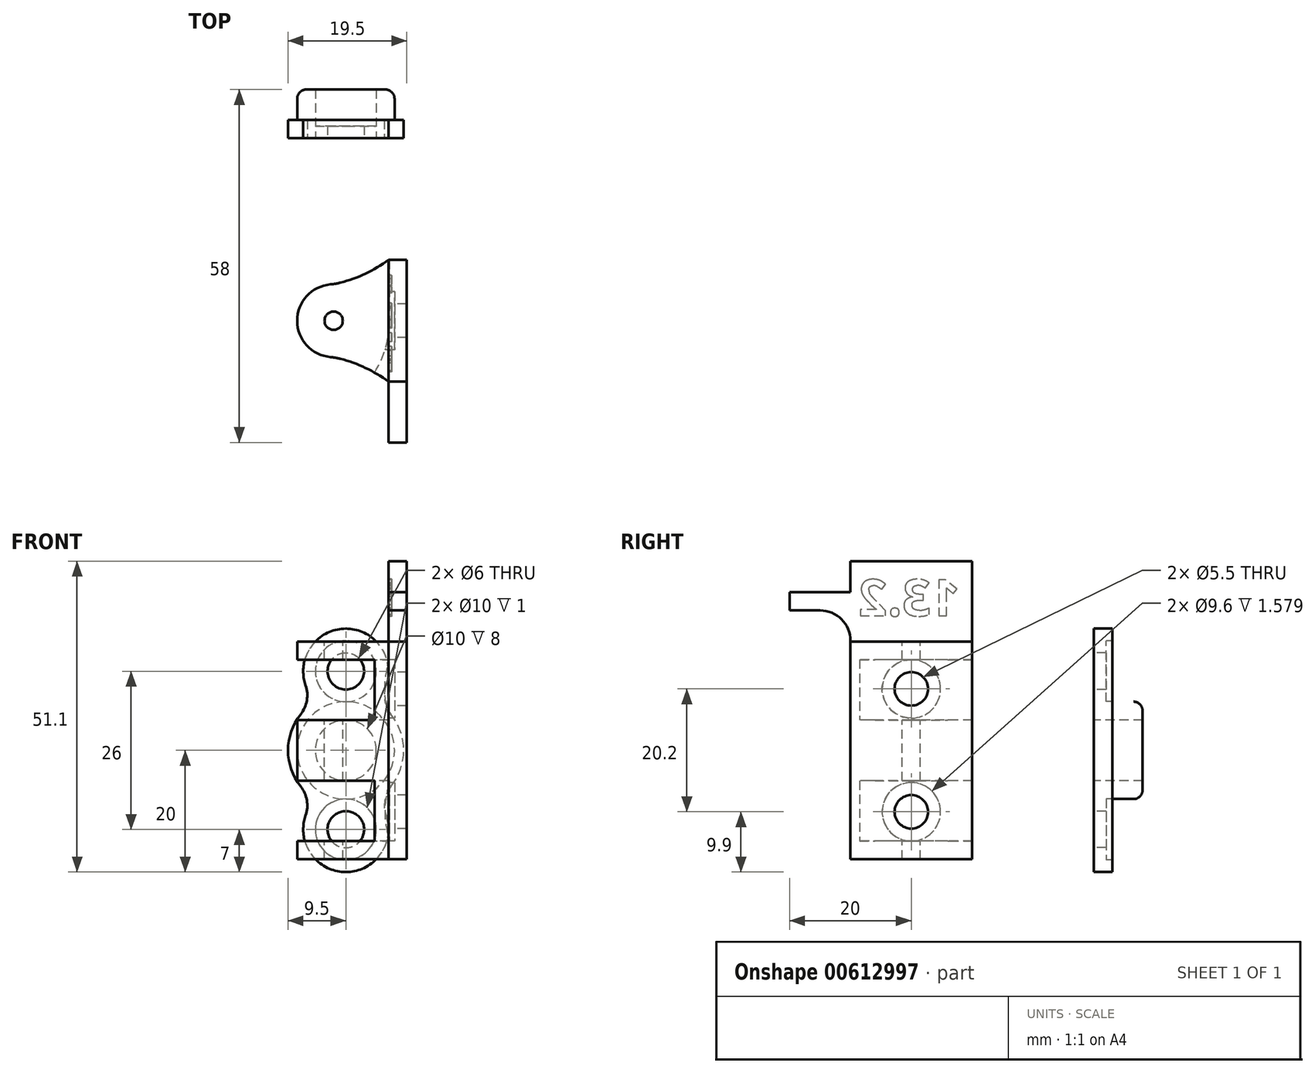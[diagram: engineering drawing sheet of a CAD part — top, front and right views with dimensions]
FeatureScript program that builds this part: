
annotation { "Feature Type Name" : "Feature", "Feature Type Description" : "" }
export const myFeature = defineFeature(function(context is Context, id is Id, definition is map)
    precondition{}
    {
        {
            var Q0;
            Q0=qCreatedBy(makeId("Top.planeOp"),FACE);
            var sketch = newSketch(context, id + "F0", { "sketchPlane" : qUnion([Q0])});
            skLineSegment(sketch, "E0", {"start": v(0, 0) * mm, "end": v(0, 17) * mm});
            skLineSegment(sketch, "E1", {"start": v(0, 17) * mm, "end": v(-3, 17) * mm});
            skLineSegment(sketch, "E2", {"start": v(-3, 17) * mm, "end": v(-3, -3) * mm});
            skLineSegment(sketch, "E3", {"start": v(-3, -3) * mm, "end": v(17, -3) * mm});
            skLineSegment(sketch, "E4", {"start": v(17, -3) * mm, "end": v(17, 0) * mm});
            skLineSegment(sketch, "E5", {"start": v(17, 0) * mm, "end": v(0, 0) * mm});
            skLineSegment(sketch, "E6", {"start": v(0, 0) * mm, "end": v(0, -3) * mm});
            skPoint(sketch, "E6.endSnap0", {"position": v(7, -3) * mm});
            skSolve(sketch);
        }
        {
            var Q0;
            Q0=makeQuery(id+"F0.imprint","IMPRINT",FACE,{"disambiguationData":[TD([[makeQuery(id+"F0.imprint","IMPRINT",EDGE,{"derivedFrom":sQuery(id+"F0.wireOp",EDGE,"E0")}),1.0]])]});
            extrude(context, id + "F1", {"entities" : qUnion([Q0]), "endBound" : BoundingType.SYMMETRIC, "depth" : 35.8 * mm, "offsetDistance" : 25 * mm});
        }
        {
            var Q0;
            Q0=makeQuery(id+"F1.opExtrude","CAP_FACE",FACE,{"disambiguationData":[OSD([sQuery(id+"F0.wireOp",EDGE,"E0"),sQuery(id+"F0.wireOp",EDGE,"E1"),sQuery(id+"F0.wireOp",EDGE,"E2"),sQuery(id+"F0.wireOp",EDGE,"E3"),sQuery(id+"F0.wireOp",EDGE,"E4"),sQuery(id+"F0.wireOp",EDGE,"E5")])],"isStart":false});
            var sketch = newSketch(context, id + "F2", { "sketchPlane" : qUnion([Q0])});
            skCircle(sketch, "E7", {"center": v(-12, 7) * mm, "radius": 6 * mm});
            skLineSegment(sketch, "E8", {"start": v(-3, 7) * mm, "end": v(-45.71, 7) * mm, "construction": true});
            skArc(sketch, "E9", {"start": v(-3, -3) * mm, "mid": v(-7.28, -0.51) * mm, "end": v(-12, 1) * mm});
            skArc(sketch, "E10.MirrorCS", {"start": v(-3, 17) * mm, "mid": v(-7.28, 14.51) * mm, "end": v(-12, 13) * mm});
            skCircle(sketch, "E11", {"center": v(-12, 7) * mm, "radius": 5 * mm, "construction": true});
            skSolve(sketch);
        }
        {
            var Q0;
            Q0 = qSketchRegion(id + "F2", true);
            var Q1;
            {var subQ5=makeQuery(id+"F1.opExtrude","CAP_EDGE",EDGE,{"disambiguationData":[OSD([sQuery(id+"F0.wireOp",EDGE,"E2")])],"isStart":false});Q1=makeQuery(id+"F2.imprint","IMPRINT",FACE,{"disambiguationData":[TD([[makeQuery(id+"F2.imprint","IMPRINT",EDGE,{"derivedFrom":subQ5}),-1.0]])]});}
            var Q2;
            Q2=makeQuery(id+"F1.opExtrude","CAP_FACE",FACE,{"disambiguationData":[OSD([sQuery(id+"F0.wireOp",EDGE,"E0"),sQuery(id+"F0.wireOp",EDGE,"E1"),sQuery(id+"F0.wireOp",EDGE,"E2"),sQuery(id+"F0.wireOp",EDGE,"E3"),sQuery(id+"F0.wireOp",EDGE,"E4"),sQuery(id+"F0.wireOp",EDGE,"E5")])],"isStart":true});
            extrude(context, id + "F3", {"entities" : qUnion([Q0, Q1]), "operationType" : NewBodyOperationType.ADD, "endBound" : BoundingType.UP_TO_SURFACE, "oppositeDirection" : true, "depth" : 25 * mm, "endBoundEntityFace" : qUnion([Q2]), "offsetDistance" : 25 * mm});
        }
        {
            var Q0;
            Q0=sQuery(id+"F2.wireOp",VERTEX,"E7.center");
            var Q1;
            Q1=qCreatedBy(makeId("Front.planeOp"),FACE);
            cPlane(context, id + "F4", {"entities" : qUnion([Q0, Q1]), "cplaneType" : CPlaneType.PLANE_POINT, "offset" : 25 * mm, "width" : 150 * mm, "height" : 150 * mm});
        }
        {
            var Q0;
            Q0=qCreatedBy(id+"F4.planeOp",FACE);
            var sketch = newSketch(context, id + "F5", { "sketchPlane" : qUnion([Q0])});
            skLineSegment(sketch, "E12", {"start": v(-27.2, 0) * mm, "end": v(27.2, 0) * mm, "construction": true});
            skLineSegment(sketch, "E13", {"start": v(-12, 17.9) * mm, "end": v(-12, -24.98) * mm, "construction": true});
            skLineSegment(sketch, "E14", {"start": v(0, 17.9) * mm, "end": v(0, -24.98) * mm, "construction": true});
            skLineSegment(sketch, "E15", {"start": v(-2.85, 17.9) * mm, "end": v(-2.85, -24.98) * mm, "construction": true});
            skLineSegment(sketch, "E16", {"start": v(-2.85, 14.9) * mm, "end": v(-19.05, 14.9) * mm});
            skLineSegment(sketch, "E17", {"start": v(-19.05, 14.9) * mm, "end": v(-19.05, 5) * mm});
            skLineSegment(sketch, "E18", {"start": v(-19.05, 5) * mm, "end": v(-2.85, 5) * mm});
            skLineSegment(sketch, "E19", {"start": v(-2.85, 5) * mm, "end": v(-2.85, 14.9) * mm});
            skLineSegment(sketch, "E20.MirrorCS", {"start": v(-19.05, -5) * mm, "end": v(-2.85, -5) * mm});
            skLineSegment(sketch, "E21.MirrorCS", {"start": v(-19.05, -14.9) * mm, "end": v(-19.05, -5) * mm});
            skLineSegment(sketch, "E22.MirrorCS", {"start": v(-2.85, -14.9) * mm, "end": v(-19.05, -14.9) * mm});
            skLineSegment(sketch, "E23.MirrorCS", {"start": v(-2.85, -17.9) * mm, "end": v(-2.85, 24.98) * mm, "construction": true});
            skLineSegment(sketch, "E24", {"start": v(0, -17.9) * mm, "end": v(-25.22, -17.9) * mm, "construction": true});
            skLineSegment(sketch, "E25", {"start": v(-2.85, -5) * mm, "end": v(-2.85, -14.9) * mm});
            skSolve(sketch);
        }
        {
            var Q0;
            Q0=makeQuery(id+"F5.imprint","IMPRINT",FACE,{"disambiguationData":[TD([[makeQuery(id+"F5.imprint","IMPRINT",EDGE,{"derivedFrom":sQuery(id+"F5.wireOp",EDGE,"E16")}),1.0]])]});
            var Q1;
            Q1=makeQuery(id+"F5.imprint","IMPRINT",FACE,{"disambiguationData":[TD([[makeQuery(id+"F5.imprint","IMPRINT",EDGE,{"derivedFrom":sQuery(id+"F5.wireOp",EDGE,"E20.MirrorCS")}),-1.0]])]});
            var Q2;
            Q2=sQuery(id+"F5.wireOp",EDGE,"E17");
            revolve(context, id + "F6", {"operationType" : NewBodyOperationType.REMOVE, "surfaceOperationType" : NewSurfaceOperationType.NEW, "entities" : qUnion([Q0, Q1]), "axis" : qUnion([Q2]), "revolveType" : RevolveType.FULL, "oppositeDirection" : true});
        }
        {
            var Q0;
            Q0=makeQuery(id+"F5.imprint","IMPRINT",FACE,{"disambiguationData":[TD([[makeQuery(id+"F5.imprint","IMPRINT",EDGE,{"derivedFrom":sQuery(id+"F5.wireOp",EDGE,"E16")}),1.0]])]});
            var Q1;
            Q1=makeQuery(id+"F5.imprint","IMPRINT",FACE,{"disambiguationData":[TD([[makeQuery(id+"F5.imprint","IMPRINT",EDGE,{"derivedFrom":sQuery(id+"F5.wireOp",EDGE,"E20.MirrorCS")}),-1.0]])]});
            extrude(context, id + "F7", {"entities" : qUnion([Q0, Q1]), "operationType" : NewBodyOperationType.REMOVE, "oppositeDirection" : true, "depth" : 25 * mm, "offsetDistance" : 25 * mm});
        }
        {
            var Q0;
            {var subQ0=sQuery(id+"F2.wireOp",EDGE,"E7");var subQ1=sQuery(id+"F2.wireOp",EDGE,"E9");Q0=makeQuery(id+"F6.boolean.opBoolean","SPLIT",EDGE,{"disambiguationData":[TD([makeQuery(id+"F6.opRevolve","SWEPT_FACE",FACE,{"disambiguationData":[OSD([sQuery(id+"F5.wireOp",EDGE,"E18")])]})])],"derivedFrom":makeQuery(id+"F3.opExtrude","SWEPT_EDGE",EDGE,{"disambiguationData":[OSD([subQ0,subQ1])]})});}
            var Q1;
            {var subQ0=sQuery(id+"F2.wireOp",EDGE,"E9");var subQ1=sQuery(id+"F2.wireOp",EDGE,"E7");Q1=makeQuery(id+"F6.boolean.opBoolean","SPLIT",EDGE,{"disambiguationData":[TD([makeQuery(id+"F6.opRevolve","SWEPT_FACE",FACE,{"disambiguationData":[OSD([sQuery(id+"F5.wireOp",EDGE,"E16")])]})])],"derivedFrom":makeQuery(id+"F3.opExtrude","SWEPT_EDGE",EDGE,{"disambiguationData":[OSD([subQ1,subQ0])]})});}
            var Q2;
            {var subQ0=sQuery(id+"F2.wireOp",EDGE,"E9");var subQ1=sQuery(id+"F2.wireOp",EDGE,"E7");Q2=makeQuery(id+"F6.boolean.opBoolean","SPLIT",EDGE,{"disambiguationData":[TD([makeQuery(id+"F6.opRevolve","SWEPT_FACE",FACE,{"disambiguationData":[OSD([sQuery(id+"F5.wireOp",EDGE,"E22.MirrorCS")])]})])],"derivedFrom":makeQuery(id+"F3.opExtrude","SWEPT_EDGE",EDGE,{"disambiguationData":[OSD([subQ1,subQ0])]})});}
            var Q3;
            {var subQ0=sQuery(id+"F2.wireOp",EDGE,"E10.MirrorCS");var subQ1=sQuery(id+"F2.wireOp",EDGE,"E7");Q3=makeQuery(id+"F6.boolean.opBoolean","SPLIT",EDGE,{"disambiguationData":[TD([makeQuery(id+"F6.opRevolve","SWEPT_FACE",FACE,{"disambiguationData":[OSD([sQuery(id+"F5.wireOp",EDGE,"E16")])]})])],"derivedFrom":makeQuery(id+"F3.opExtrude","SWEPT_EDGE",EDGE,{"disambiguationData":[OSD([subQ1,subQ0])]})});}
            var Q4;
            {var subQ0=sQuery(id+"F2.wireOp",EDGE,"E7");var subQ1=sQuery(id+"F2.wireOp",EDGE,"E10.MirrorCS");Q4=makeQuery(id+"F6.boolean.opBoolean","SPLIT",EDGE,{"disambiguationData":[TD([makeQuery(id+"F6.opRevolve","SWEPT_FACE",FACE,{"disambiguationData":[OSD([sQuery(id+"F5.wireOp",EDGE,"E18")])]})])],"derivedFrom":makeQuery(id+"F3.opExtrude","SWEPT_EDGE",EDGE,{"disambiguationData":[OSD([subQ0,subQ1])]})});}
            var Q5;
            {var subQ0=sQuery(id+"F2.wireOp",EDGE,"E10.MirrorCS");var subQ1=sQuery(id+"F2.wireOp",EDGE,"E7");Q5=makeQuery(id+"F6.boolean.opBoolean","SPLIT",EDGE,{"disambiguationData":[TD([makeQuery(id+"F6.opRevolve","SWEPT_FACE",FACE,{"disambiguationData":[OSD([sQuery(id+"F5.wireOp",EDGE,"E22.MirrorCS")])]})])],"derivedFrom":makeQuery(id+"F3.opExtrude","SWEPT_EDGE",EDGE,{"disambiguationData":[OSD([subQ1,subQ0])]})});}
            fillet(context, id + "F8", {"entities" : qUnion([Q0, Q1, Q2, Q3, Q4, Q5]), "radius" : 10 * mm, "tangentPropagation" : true, "allowEdgeOverflow" : false});
        }
        {
            var Q0;
            Q0=qCreatedBy(makeId("Right.planeOp"),FACE);
            cPlane(context, id + "F9", {"entities" : qUnion([Q0]), "cplaneType" : CPlaneType.OFFSET, "offset" : 10 * mm, "oppositeDirection" : true, "width" : 150 * mm, "height" : 150 * mm});
        }
        {
            var Q0;
            Q0=qCreatedBy(id+"F9.planeOp",FACE);
            var sketch = newSketch(context, id + "F10", { "sketchPlane" : qUnion([Q0])});
            skLineSegment(sketch, "E26", {"start": v(7, 17.9) * mm, "end": v(7, -17.9) * mm});
            skLineSegment(sketch, "E27", {"start": v(-3, 10.1) * mm, "end": v(17, 10.1) * mm});
            skLineSegment(sketch, "E28", {"start": v(-3, -10.1) * mm, "end": v(17, -10.1) * mm});
            skPoint(sketch, "E29.positionSnap0", {"position": v(7, 10.1) * mm});
            skLineSegment(sketch, "E30", {"start": v(-3, 0) * mm, "end": v(17, 0) * mm});
            skPoint(sketch, "E31", {"position": v(7, 0) * mm});
            skPoint(sketch, "E32", {"position": v(7, -10.1) * mm});
            skSolve(sketch);
        }
        {
            var Q0;
            Q0=sQuery(id+"F10.wireOp",VERTEX,"E29.positionSnap0");
            var Q1;
            Q1=sQuery(id+"F10.wireOp",VERTEX,"E32");
            var Q2;
            Q2=makeQuery(id+"F1.opExtrude","SWEPT_BODY",BODY,{"disambiguationData":[OSD([sQuery(id+"F0.wireOp",EDGE,"E0"),sQuery(id+"F0.wireOp",EDGE,"E1"),sQuery(id+"F0.wireOp",EDGE,"E2"),sQuery(id+"F0.wireOp",EDGE,"E3"),sQuery(id+"F0.wireOp",EDGE,"E4"),sQuery(id+"F0.wireOp",EDGE,"E5")])]});
            hole(context, id + "F11", {"style" : HoleStyle.C_BORE, "endStyle" : HoleEndStyle.BLIND, "oppositeDirection" : true, "holeDiameter" : 5.5 * mm, "cBoreDiameter" : 9.6 * mm, "cBoreDepth" : 8 * mm, "majorDiameter" : 5 * mm, "holeDepth" : 15 * mm, "isTappedThrough" : true, "tappedDepth" : 12 * mm, "tapClearance" : 3, "startFromSketch" : true, "locations" : qUnion([Q0, Q1]), "scope" : qUnion([Q2])});
        }
        {
            var Q0;
            Q0=sQuery(id+"F2.wireOp",VERTEX,"E7.center");
            var Q1;
            Q1=makeQuery(id+"F1.opExtrude","SWEPT_BODY",BODY,{"disambiguationData":[OSD([sQuery(id+"F0.wireOp",EDGE,"E0"),sQuery(id+"F0.wireOp",EDGE,"E1"),sQuery(id+"F0.wireOp",EDGE,"E2"),sQuery(id+"F0.wireOp",EDGE,"E3"),sQuery(id+"F0.wireOp",EDGE,"E4"),sQuery(id+"F0.wireOp",EDGE,"E5")])]});
            hole(context, id + "F12", {"style" : HoleStyle.C_BORE, "endStyle" : HoleEndStyle.BLIND, "holeDiameter" : 3 * mm, "cBoreDiameter" : 3 * mm, "cBoreDepth" : 1 * mm, "majorDiameter" : 5 * mm, "holeDepth" : 36 * mm, "isTappedThrough" : true, "tappedDepth" : 12 * mm, "tapClearance" : 3, "locations" : qUnion([Q0]), "scope" : qUnion([Q1])});
        }
        {
            var Q0;
            Q0=makeQuery(id+"FeZ5zbQZLyVp1cH_1.boolean.opBoolean","COPY",FACE,{"derivedFrom":makeQuery(id+"FeZ5zbQZLyVp1cH_1.opExtrude","CAP_FACE",FACE,{"disambiguationData":[OSD([sQuery(id+"FttwEAgkm9gSssU_1.wireOp",EDGE,"wkAEEsgB-SSld-rnjB-hXSZ-VIMV09JZoIiA"),sQuery(id+"FttwEAgkm9gSssU_1.wireOp",EDGE,"v8r9AJHU-UUQQ-qF1N-W90g-7rf2DQYjYhxg"),sQuery(id+"FttwEAgkm9gSssU_1.wireOp",EDGE,"8OySchBC-DH8u-Lw9Y-1EKe-5hH2m8zCJ6XQ"),sQuery(id+"FttwEAgkm9gSssU_1.wireOp",EDGE,"ENTNz0sq-afUB-d1Q0-3b3s-MBKBizV5C8en"),sQuery(id+"FttwEAgkm9gSssU_1.wireOp",EDGE,"CpcCRfJK-ipJY-PiRr-u0bL-AVLWpuY7FLgk"),sQuery(id+"FttwEAgkm9gSssU_1.wireOp",EDGE,"ZY0SYlgB-TEKi-9KMc-JPQQ-Eyn3OuHgfAgN")])],"isStart":true})});
            var Q1;
            Q1=makeQuery(id+"F1.opExtrude","SWEPT_FACE",FACE,{"disambiguationData":[OSD([sQuery(id+"F0.wireOp",EDGE,"E1")])]});
            cPlane(context, id + "F13", {"entities" : qUnion([Q0, Q1]), "cplaneType" : CPlaneType.OFFSET, "offset" : 20 * mm, "width" : 150 * mm, "height" : 150 * mm});
        }
        {
            var Q0;
            Q0=qCreatedBy(id+"F13.planeOp",FACE);
            var sketch = newSketch(context, id + "F14", { "sketchPlane" : qUnion([Q0])});
            skCircle(sketch, "E33", {"center": v(10, 13) * mm, "radius": 3 * mm});
            skCircle(sketch, "E34", {"center": v(10, -13) * mm, "radius": 3 * mm});
            skCircle(sketch, "E35", {"center": v(10, 0) * mm, "radius": 5 * mm});
            skArc(sketch, "E36", {"start": v(17.42, -5.93) * mm, "mid": v(19.5, 0) * mm, "end": v(17.42, 5.93) * mm});
            skArc(sketch, "E37", {"start": v(16.6, 10.7) * mm, "mid": v(10, 20) * mm, "end": v(3.4, 10.7) * mm});
            skArc(sketch, "E38", {"start": v(3.4, -10.7) * mm, "mid": v(10, -20) * mm, "end": v(16.6, -10.7) * mm});
            skArc(sketch, "E39.trimOffspring", {"start": v(2.58, 5.93) * mm, "mid": v(0.5, 0) * mm, "end": v(2.58, -5.93) * mm});
            skPoint(sketch, "E40.visualSharp", {"position": v(5.01, 8.09) * mm});
            skArc(sketch, "E40.filletArc", {"start": v(2.58, 5.93) * mm, "mid": v(3.6, 8.2) * mm, "end": v(3.4, 10.7) * mm});
            skPoint(sketch, "E41.visualSharp", {"position": v(5.01, -8.09) * mm});
            skArc(sketch, "E41.filletArc", {"start": v(3.4, -10.7) * mm, "mid": v(3.6, -8.2) * mm, "end": v(2.58, -5.93) * mm});
            skPoint(sketch, "E42.visualSharp", {"position": v(14.99, -8.09) * mm});
            skArc(sketch, "E42.filletArc", {"start": v(17.42, -5.93) * mm, "mid": v(16.4, -8.2) * mm, "end": v(16.6, -10.7) * mm});
            skPoint(sketch, "E43.visualSharp", {"position": v(14.99, 8.09) * mm});
            skArc(sketch, "E43.filletArc", {"start": v(16.6, 10.7) * mm, "mid": v(16.4, 8.2) * mm, "end": v(17.42, 5.93) * mm});
            skSolve(sketch);
        }
        {
            var Q0;
            Q0=makeQuery(id+"F14.imprint","IMPRINT",FACE,{"disambiguationData":[TD([[makeQuery(id+"F14.imprint","IMPRINT",EDGE,{"derivedFrom":sQuery(id+"F14.wireOp",EDGE,"E33")}),-1.0]])]});
            extrude(context, id + "F15", {"entities" : qUnion([Q0]), "operationType" : NewBodyOperationType.ADD, "depth" : 3 * mm, "offsetDistance" : 25 * mm});
        }
        {
            var Q0;
            Q0=makeQuery(id+"F15.opExtrude","CAP_FACE",FACE,{"disambiguationData":[OSD([sQuery(id+"F14.wireOp",EDGE,"E33"),sQuery(id+"F14.wireOp",EDGE,"E34"),sQuery(id+"F14.wireOp",EDGE,"E35"),sQuery(id+"F14.wireOp",EDGE,"E36"),sQuery(id+"F14.wireOp",EDGE,"E37"),sQuery(id+"F14.wireOp",EDGE,"E38"),sQuery(id+"F14.wireOp",EDGE,"E39.trimOffspring"),sQuery(id+"F14.wireOp",EDGE,"E40.filletArc"),sQuery(id+"F14.wireOp",EDGE,"E41.filletArc"),sQuery(id+"F14.wireOp",EDGE,"E42.filletArc"),sQuery(id+"F14.wireOp",EDGE,"E43.filletArc")])],"isStart":false});
            var sketch = newSketch(context, id + "F16", { "sketchPlane" : qUnion([Q0])});
            skCircle(sketch, "E44", {"center": v(10, 0) * mm, "radius": 5 * mm});
            skCircle(sketch, "E45", {"center": v(10, 0) * mm, "radius": 8 * mm});
            skCircle(sketch, "E46", {"center": v(10, 13) * mm, "radius": 5 * mm});
            skCircle(sketch, "E47", {"center": v(10, -13) * mm, "radius": 5 * mm});
            skSolve(sketch);
        }
        {
            var Q0;
            Q0=makeQuery(id+"F16.imprint","IMPRINT",FACE,{"disambiguationData":[TD([[makeQuery(id+"F16.imprint","IMPRINT",EDGE,{"derivedFrom":sQuery(id+"F16.wireOp",EDGE,"E44")}),-1.0]])]});
            extrude(context, id + "F17", {"entities" : qUnion([Q0]), "operationType" : NewBodyOperationType.ADD, "depth" : 5 * mm, "offsetDistance" : 25 * mm});
        }
        {
            var Q0;
            Q0=makeQuery(id+"F17.opExtrude","CAP_EDGE",EDGE,{"disambiguationData":[OSD([sQuery(id+"F16.wireOp",EDGE,"E45")])],"isStart":true});
            var Q1;
            Q1=makeQuery(id+"F17.opExtrude","CAP_EDGE",EDGE,{"disambiguationData":[OSD([sQuery(id+"F16.wireOp",EDGE,"E45")])],"isStart":false});
            fillet(context, id + "F18", {"entities" : qUnion([Q0, Q1]), "radius" : 1.5 * mm, "tangentPropagation" : true, "allowEdgeOverflow" : false});
        }
        {
            var Q0;
            Q0=makeQuery(id+"F16.imprint","IMPRINT",FACE,{"disambiguationData":[TD([[makeQuery(id+"F16.imprint","IMPRINT",EDGE,{"derivedFrom":sQuery(id+"F16.wireOp",EDGE,"E46")}),1.0]])]});
            var Q1;
            Q1=makeQuery(id+"F16.imprint","IMPRINT",FACE,{"disambiguationData":[TD([[makeQuery(id+"F16.imprint","IMPRINT",EDGE,{"derivedFrom":sQuery(id+"F16.wireOp",EDGE,"E47")}),1.0]])]});
            extrude(context, id + "F19", {"entities" : qUnion([Q0, Q1]), "operationType" : NewBodyOperationType.REMOVE, "depth" : 3 * mm, "offsetDistance" : 25 * mm, "hasSecondDirection" : true, "secondDirectionOppositeDirection" : true, "secondDirectionDepth" : 1 * mm});
        }
        {
            var Q0;
            Q0=makeQuery(id+"F2.imprint","IMPRINT",FACE,{"disambiguationData":[TD([[makeQuery(id+"F2.imprint","IMPRINT",EDGE,{"derivedFrom":makeQuery(id+"F1.opExtrude","CAP_EDGE",EDGE,{"disambiguationData":[OSD([sQuery(id+"F0.wireOp",EDGE,"E1")])],"isStart":false})}),1.0]])]});
            var sketch = newSketch(context, id + "F20", { "sketchPlane" : qUnion([Q0])});
            skLineSegment(sketch, "E48.bottom", {"start": v(0, 17) * mm, "end": v(-3, 17) * mm});
            skLineSegment(sketch, "E48.top", {"start": v(0, -3) * mm, "end": v(-3, -3) * mm});
            skLineSegment(sketch, "E48.left", {"start": v(0, 17) * mm, "end": v(0, -3) * mm});
            skLineSegment(sketch, "E48.right", {"start": v(-3, 17) * mm, "end": v(-3, -3) * mm});
            skSolve(sketch);
        }
        {
            var Q0;
            Q0 = qSketchRegion(id + "F20", true);
            var Q1;
            {var subQ0=sQuery(id+"F20.wireOp",EDGE,"E48.top");Q1=makeQuery(id+"F20.imprint","IMPRINT",FACE,{"disambiguationData":[TD([[makeQuery(id+"F20.imprint","IMPRINT",EDGE,{"derivedFrom":subQ0}),-1.0]])]});}
            extrude(context, id + "F21", {"entities" : qUnion([Q0, Q1]), "depth" : 13.2 * mm, "offsetDistance" : 25 * mm});
        }
        {
            var Q0;
            Q0=makeQuery(id+"F21.opExtrude","SWEPT_FACE",FACE,{"disambiguationData":[OSD([sQuery(id+"F20.wireOp",EDGE,"E48.top")])]});
            var sketch = newSketch(context, id + "F22", { "sketchPlane" : qUnion([Q0])});
            skLineSegment(sketch, "E49.bottom", {"start": v(-3, 26) * mm, "end": v(0, 26) * mm});
            skLineSegment(sketch, "E49.top", {"start": v(-3, 23) * mm, "end": v(0, 23) * mm});
            skLineSegment(sketch, "E49.left", {"start": v(-3, 26) * mm, "end": v(-3, 23) * mm});
            skLineSegment(sketch, "E49.right", {"start": v(0, 26) * mm, "end": v(0, 23) * mm});
            skPoint(sketch, "E49.middle", {"position": v(-1.5, 24.5) * mm});
            skPoint(sketch, "E49.middle.positionSnap0", {"position": v(-3, 24.5) * mm});
            skPoint(sketch, "E49.middle.positionSnap1", {"position": v(-1.5, 31.1) * mm});
            skPoint(sketch, "E49.centerSnap0", {"position": v(-3, 24.5) * mm});
            skPoint(sketch, "E49.centerSnap1", {"position": v(-1.5, 31.1) * mm});
            skSolve(sketch);
        }
        {
            var Q0;
            Q0=makeQuery(id+"F22.imprint","IMPRINT",FACE,{"disambiguationData":[TD([[makeQuery(id+"F22.imprint","IMPRINT",EDGE,{"derivedFrom":sQuery(id+"F22.wireOp",EDGE,"E49.bottom")}),-1.0]])]});
            extrude(context, id + "F23", {"entities" : qUnion([Q0]), "operationType" : NewBodyOperationType.ADD, "depth" : 10 * mm, "offsetDistance" : 25 * mm});
        }
        {
            var Q0;
            Q0=makeQuery(id+"F23.opExtrude","CAP_EDGE",EDGE,{"disambiguationData":[OSD([sQuery(id+"F22.wireOp",EDGE,"E49.bottom")])],"isStart":true});
            var Q1;
            Q1=makeQuery(id+"F23.opExtrude","CAP_EDGE",EDGE,{"disambiguationData":[OSD([sQuery(id+"F22.wireOp",EDGE,"E49.top")])],"isStart":true});
            fillet(context, id + "F24", {"entities" : qUnion([Q0, Q1]), "radius" : 5 * mm, "tangentPropagation" : true, "allowEdgeOverflow" : false});
        }
        {
            var Q0;
            Q0=makeQuery(id+"F23.boolean.opBoolean","MERGE",FACE,{"derivedFrom":[makeQuery(id+"F21.opExtrude","SWEPT_FACE",FACE,{"disambiguationData":[OSD([sQuery(id+"F20.wireOp",EDGE,"E48.right")])]}),makeQuery(id+"F23.opExtrude","SWEPT_FACE",FACE,{"disambiguationData":[OSD([sQuery(id+"F22.wireOp",EDGE,"E49.left")])]})]});
            var sketch = newSketch(context, id + "F25", { "sketchPlane" : qUnion([Q0])});
            skText(sketch, "E50", { "text": "13.2 ", "fontName": "OpenSans-Bold.ttf"});
            const initialGuessF25  = {"E50": [-0.01499, 0.0221, 1, 0, 0.006]};
            skSetInitialGuess(sketch, initialGuessF25);
            skSolve(sketch);
        }
        {
            var Q0;
            Q0 = qSketchRegion(id + "F25", true);
            var Q1;
            Q1=makeQuery(id+"F25.imprint","IMPRINT",FACE,{"disambiguationData":[TD([[makeQuery(id+"F25.imprint","IMPRINT",EDGE,{"derivedFrom":sQuery(id+"F25.wireOp",EDGE,"E50.sketch_text.stroke-0")}),-1.0]])]});
            extrude(context, id + "F26", {"entities" : qUnion([Q0, Q1]), "operationType" : NewBodyOperationType.REMOVE, "oppositeDirection" : true, "depth" : 0.5 * mm, "offsetDistance" : 25 * mm});
        }
    });
